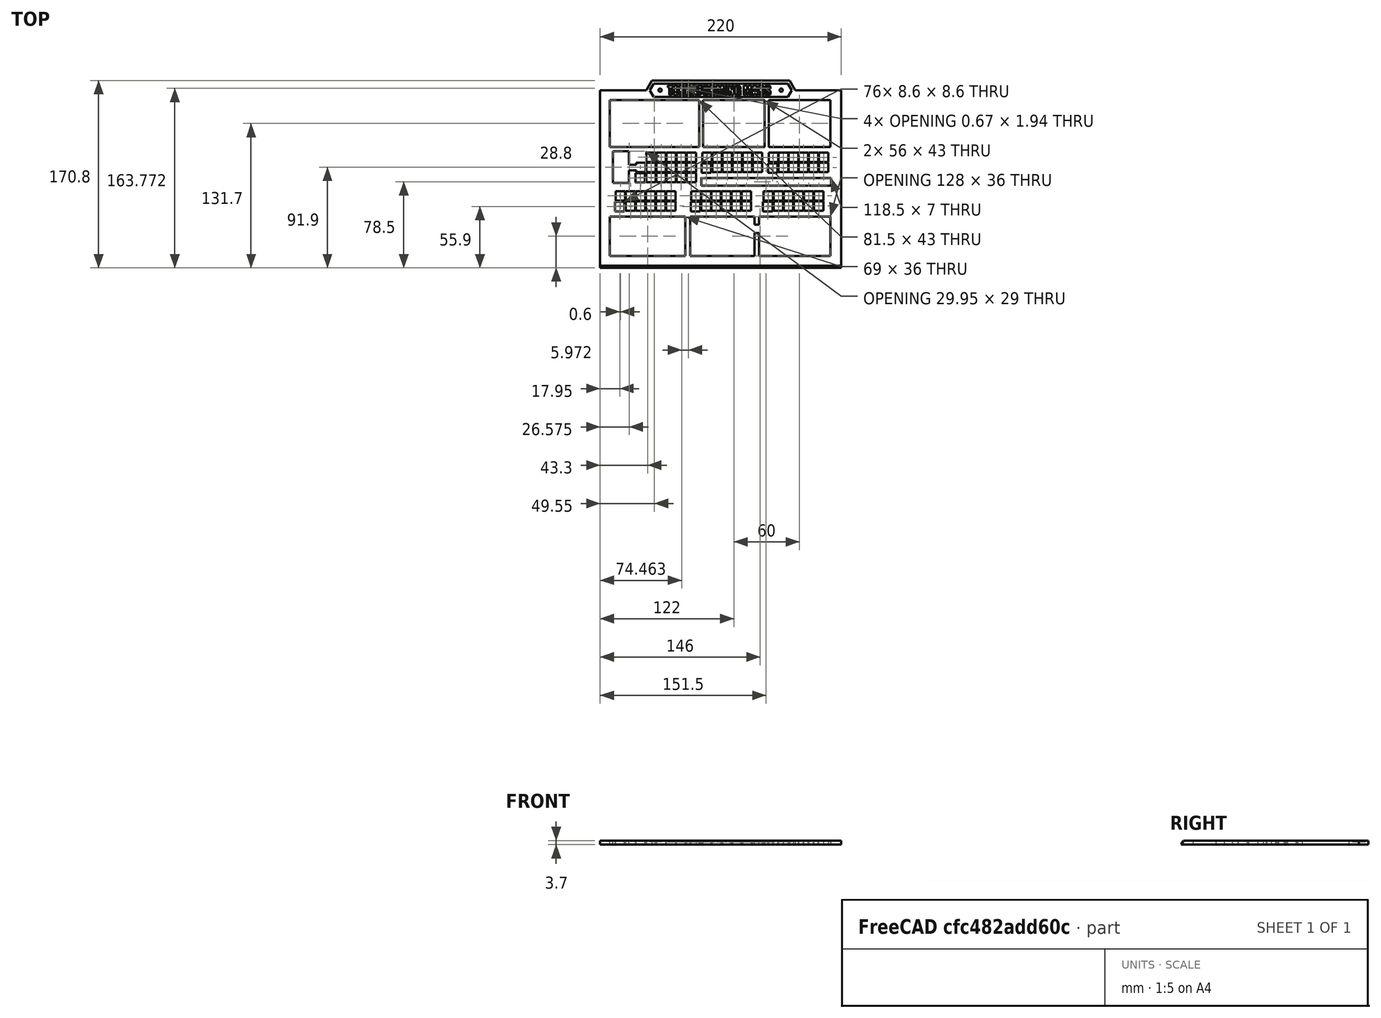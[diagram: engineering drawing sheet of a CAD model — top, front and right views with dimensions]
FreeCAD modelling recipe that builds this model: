
FCSTD DOCUMENT  (FreeCAD 0.21R33668 +26 (Git))
Label: overlay-full-v2
License: All rights reserved
LicenseURL: https://en.wikipedia.org/wiki/All_rights_reserved
objects: Sketcher::SketchObject×5, PartDesign::Pad×4, Part::Feature×2, PartDesign::Pocket×2, Mesh::Feature×1, Part::Refine×1, PartDesign::FeatureBase×1, Part::Part2DObjectPython×1, PartDesign::Body×1, Part::Extrusion×1
note: 24 computed .brp shape members not serialized (recipe doc carries the construction recipe); baked Part::Feature solids carry a one-line shape summary decoded from their .brp

FEATURE [Mesh::Feature] Terraforming_Mars_overlay
FEATURE [Part::Feature] Terraforming_Mars_overlay001
  shape: bbox 208 x 148 x 3.7 mm, 1736 faces, 0 solids (baked)
FEATURE [Part::Feature] Terraforming_Mars_overlay001_solid  label="Terraforming_Mars_overlay001 (Solid)"
  shape: bbox 208 x 148 x 3.7 mm, 1736 faces (baked)
FEATURE [Part::Refine] Terraforming_Mars_overlay001_solid001  label="Terraforming_Mars_overlay001 (Solid)001"
  Source = -> Terraforming_Mars_overlay001_solid
FEATURE [PartDesign::FeatureBase] BaseFeature
  BaseFeature = -> Terraforming_Mars_overlay001_solid001
FEATURE [Sketcher::SketchObject] Sketch
  ExternalGeometry = -> [BaseFeature]
  FullyConstrained = true
  MapMode = 5
  Placement = pos=(0,0,3.7) rot=(0,0,1;0rad)
  Support = -> [BaseFeature]
  sketch-geometry (8):
    g0: LineSegment StartX=6 StartY=154 StartZ=0 EndX=214 EndY=154 EndZ=0
    g1: LineSegment StartX=214 StartY=154 StartZ=0 EndX=214 EndY=6 EndZ=0
    g2: LineSegment StartX=214 StartY=6 StartZ=0 EndX=6 EndY=6 EndZ=0
    g3: LineSegment StartX=6 StartY=6 StartZ=0 EndX=6 EndY=154 EndZ=0
    g4: LineSegment StartX=0 StartY=160 StartZ=0 EndX=220 EndY=160 EndZ=0
    g5: LineSegment StartX=220 StartY=160 StartZ=0 EndX=220 EndY=0 EndZ=0
    g6: LineSegment StartX=220 StartY=0 StartZ=0 EndX=0 EndY=0 EndZ=0
    g7: LineSegment StartX=0 StartY=0 StartZ=0 EndX=0 EndY=160 EndZ=0
  constraints (22):
    c: Coincident(g0,g1)
    c: Coincident(g1,g2)
    c: Coincident(g2,g3)
    c: Coincident(g3,g0)
    c: Horizontal(g0)
    c: Horizontal(g2)
    c: Vertical(g1)
    c: Vertical(g3)
    c: Coincident(g0,g-3)
    c: Coincident(g1,g-4)
    c: Coincident(g4,g5)
    c: Coincident(g5,g6)
    c: Coincident(g6,g7)
    c: Coincident(g7,g4)
    c: Horizontal(g4)
    c: Horizontal(g6)
    c: Vertical(g5)
    c: Vertical(g7)
    c: DistanceX(g4,g0) = 6
    c: DistanceX(g0,g4) = 6
    c: DistanceY(g0,g4) = 6
    c: DistanceY(g5,g1) = 6
FEATURE [PartDesign::Pad] Pad
  BaseFeature = -> BaseFeature
  Direction = (0,0,1)
  Length = 10
  Length2 = 10
  Profile = -> Sketch
  ReferenceAxis = -> Sketch [N_Axis]
  Type = 3
  UpToFace = -> BaseFeature [Face1]
FEATURE [Sketcher::SketchObject] Sketch001
  ExternalGeometry = -> [Pad]
  FullyConstrained = true
  MapMode = 5
  Placement = pos=(0,0,3.7) rot=(0,0,1;0rad)
  Support = -> [Pad]
  sketch-geometry (5):
    g0: GeomPoint X=110 Y=160 Z=0
    g1: LineSegment StartX=42 StartY=160 StartZ=0 EndX=47.0807 EndY=168.8 EndZ=0
    g2: LineSegment StartX=47.0807 StartY=168.8 StartZ=0 EndX=172.919 EndY=168.8 EndZ=0
    g3: LineSegment StartX=172.919 StartY=168.8 StartZ=0 EndX=178 EndY=160 EndZ=0
    g4: LineSegment StartX=178 StartY=160 StartZ=0 EndX=42 EndY=160 EndZ=0
  constraints (13):
    c: Symmetric(g-3,g-3,g0)
    c: Coincident(g1,g2)
    c: Horizontal(g2)
    c: Coincident(g2,g3)
    c: Coincident(g3,g4)
    c: Coincident(g4,g1)
    c: Angle(g1,g4,g1) = 2.0944
    c: Angle(g4,g3,g3) = 2.0944
    c: DistanceY(g1,g1) = 8.8
    c: PointOnObject(g1,g-3)
    c: DistanceX(g-3,g1) = 42
    c: DistanceX(g3,g-3) = 42
    c: PointOnObject(g3,g-3)
FEATURE [PartDesign::Pad] Pad001
  BaseFeature = -> Pad
  Direction = (0,0,1)
  Length = 10
  Length2 = 10
  Profile = -> Sketch001
  ReferenceAxis = -> Sketch001 [N_Axis]
  Type = 3
  UpToFace = -> Pad [Face2]
FEATURE [Sketcher::SketchObject] Sketch002
  ExternalGeometry = -> [Pad001]
  FullyConstrained = true
  MapMode = 5
  Placement = pos=(0,0,3.7) rot=(0,0,1;0rad)
  Support = -> [Pad001]
  sketch-geometry (7):
    g0: GeomPoint X=110 Y=160 Z=0
    g1: LineSegment StartX=45.2332 StartY=160 StartZ=0 EndX=48.6973 EndY=166 EndZ=0
    g2: LineSegment StartX=48.6973 StartY=166 StartZ=0 EndX=171.303 EndY=166 EndZ=0
    g3: LineSegment StartX=171.303 StartY=166 StartZ=0 EndX=174.767 EndY=160 EndZ=0
    g4: LineSegment StartX=174.767 StartY=160 StartZ=0 EndX=171.303 EndY=154 EndZ=0
    g5: LineSegment StartX=171.303 StartY=154 StartZ=0 EndX=48.6973 EndY=154 EndZ=0
    g6: LineSegment StartX=48.6973 StartY=154 StartZ=0 EndX=45.2332 EndY=160 EndZ=0
  constraints (17):
    c: Symmetric(g-4,g-4,g0)
    c: PointOnObject(g1,g-4)
    c: Coincident(g1,g2)
    c: Horizontal(g2)
    c: Coincident(g2,g3)
    c: PointOnObject(g3,g-4)
    c: Coincident(g3,g4)
    c: PointOnObject(g4,g-5)
    c: Coincident(g4,g5)
    c: Coincident(g5,g6)
    c: Coincident(g6,g1)
    c: Parallel(g1,g-6)
    c: Symmetric(g5,g1,g-4)
    c: Symmetric(g4,g2,g-4)
    c: Parallel(g3,g-7)
    c: Distance(g1,g-6) = 2.8
    c: Distance(g2,g-7) = 2.8
FEATURE [PartDesign::Pocket] Pocket
  BaseFeature = -> Pad001
  Direction = (0,0,-1)
  Length = 1
  Length2 = 5
  Profile = -> Sketch002
  ReferenceAxis = -> Sketch002 [N_Axis]
  Type = 0
FEATURE [Part::Part2DObjectPython] ShapeString  # Draft 2D object (typed FeaturePython)
  FontFile = <path>
  MakeFace = true
  Placement = pos=(61.7,155.5,2.7) rot=(0,0,1;0rad)
  Size = 9
  String = TERRAFORMING MARS
  Tracking = 0
FEATURE [Sketcher::SketchObject] Sketch003
  ExternalGeometry = -> [Pocket]
  FullyConstrained = true
  MapMode = 5
  Placement = pos=(0,0,2.7) rot=(0,0,1;0rad)
  Support = -> [Pocket]
  sketch-geometry (3):
    g0: LineSegment StartX=45.2332 StartY=160 StartZ=0 EndX=174.767 EndY=160 EndZ=0
    g1: Circle CenterX=54.7332 CenterY=160 CenterZ=0 NormalX=0 NormalY=0 NormalZ=1 AngleXU=0 Radius=1.5
    g2: Circle CenterX=165.267 CenterY=160 CenterZ=0 NormalX=0 NormalY=0 NormalZ=1 AngleXU=0 Radius=1.5
  constraints (8):
    c: Coincident(g0,g-3)
    c: Coincident(g0,g-4)
    c: PointOnObject(g1,g0)
    c: PointOnObject(g2,g0)
    c: Diameter(g2) = 3
    c: Diameter(g1) = 3
    c: DistanceX(g0,g1) = 9.5
    c: DistanceX(g2,g0) = 9.5
FEATURE [PartDesign::Pad] Pad002
  BaseFeature = -> Pocket
  Direction = (0,0,1)
  Length = 1
  Length2 = 10
  Profile = -> Sketch003
  ReferenceAxis = -> Sketch003 [N_Axis]
  Type = 0
FEATURE [PartDesign::Pad] Pad003
  BaseFeature = -> Pad002
  Direction = (0,-1,0)
  Length = 2
  Length2 = 10
  Profile = -> Pad002 [Face352]
  Type = 0
FEATURE [Sketcher::SketchObject] Sketch004
  ExternalGeometry = -> [Pad003]
  FullyConstrained = true
  MapMode = 5
  Placement = pos=(220,0,0) rot=(0.57735,0.57735,0.57735;2.0944rad)
  Support = -> [Pad003]
  sketch-geometry (3):
    g0: LineSegment StartX=0 StartY=3.7 StartZ=0 EndX=-2 EndY=0 EndZ=0
    g1: LineSegment StartX=-2 StartY=0 StartZ=0 EndX=-2 EndY=3.7 EndZ=0
    g2: LineSegment StartX=-2 StartY=3.7 StartZ=0 EndX=0 EndY=3.7 EndZ=0
  constraints (6):
    c: Coincident(g-4,g0)
    c: Coincident(g0,g-3)
    c: Coincident(g0,g1)
    c: Coincident(g1,g-4)
    c: Coincident(g1,g2)
    c: Coincident(g2,g0)
FEATURE [PartDesign::Pocket] Pocket001
  BaseFeature = -> Pad003
  Direction = (-1,0,0)
  Length = 5
  Length2 = 5
  Profile = -> Sketch004
  ReferenceAxis = -> Sketch004 [N_Axis]
  Type = 1
FEATURE [PartDesign::Body] Body
  BaseFeature = -> Terraforming_Mars_overlay001_solid001
  Group = -> [BaseFeature,Sketch,Pad,Sketch001,Pad001,Sketch002,Pocket,Sketch003,Pad002,Pad003,Sketch004,Pocket001]
  Origin = -> Origin
  Tip = -> Pocket001
FEATURE [Part::Extrusion] Extrude
  Base = -> ShapeString
  Dir = (0,0,1)
  DirMode = 2
  FaceMakerClass = Part::FaceMakerBullseye
  LengthFwd = 1
  LengthRev = 0
  Solid = false
  Symmetric = false
note: 1 file-system path scrubbed to <path> (originals preserved in the JSON sidecar)
